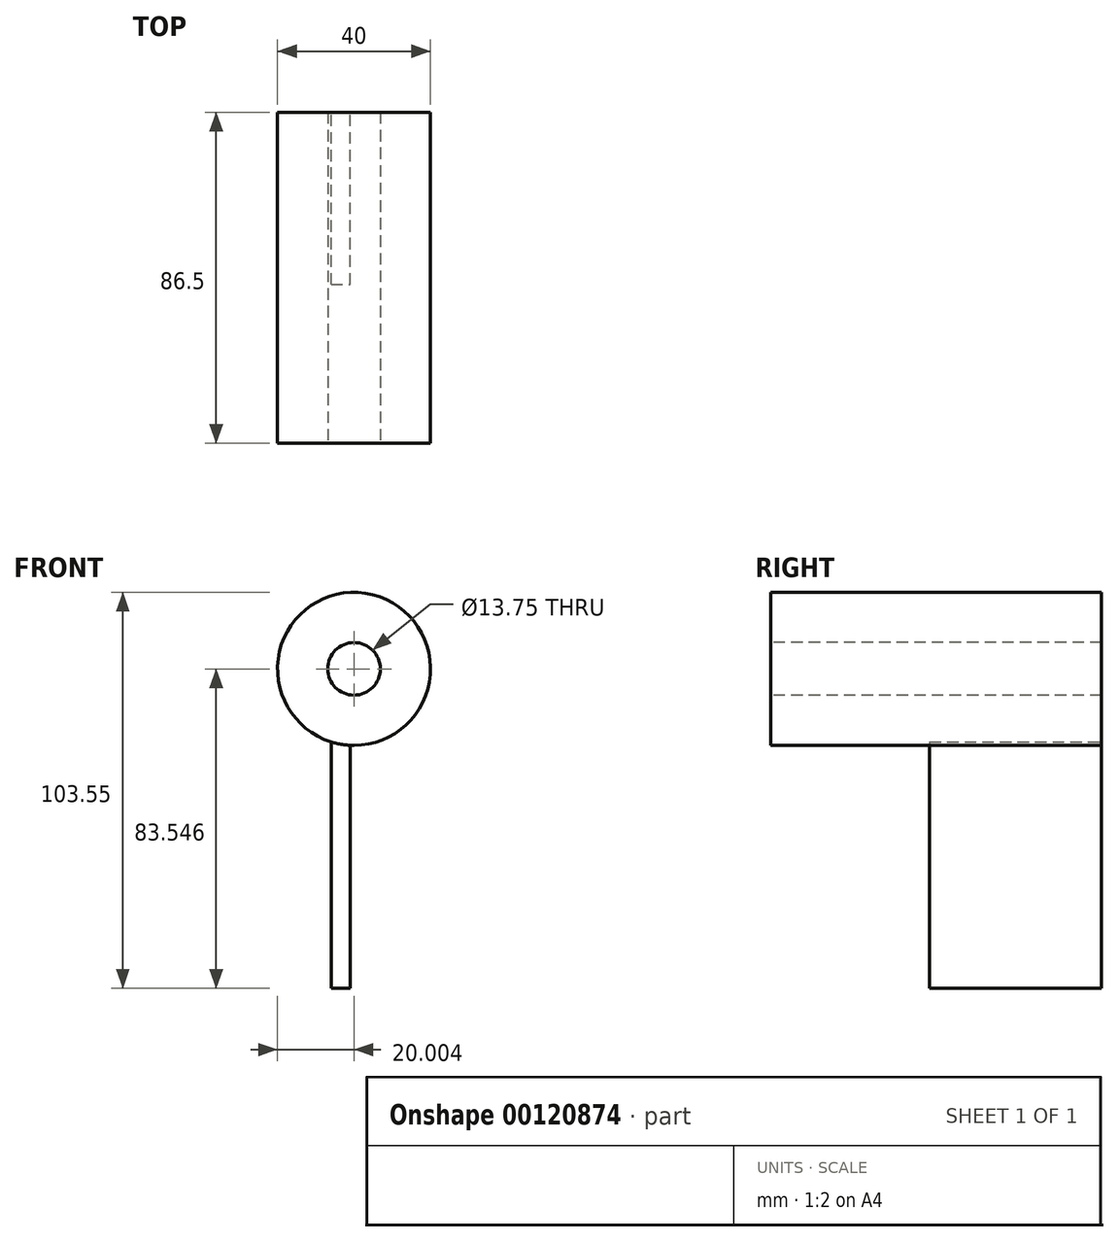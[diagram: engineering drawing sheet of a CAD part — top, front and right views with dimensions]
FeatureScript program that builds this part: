
annotation { "Feature Type Name" : "Feature", "Feature Type Description" : "" }
export const myFeature = defineFeature(function(context is Context, id is Id, definition is map)
    precondition{}
    {
        {
            var Q0;
            Q0=qCreatedBy(makeId("Front.planeOp"),FACE);
            var sketch = newSketch(context, id + "F0", { "sketchPlane" : qUnion([Q0])});
            skCircle(sketch, "E0", {"center": v(-25.19, 35.43) * mm, "radius": 20 * mm});
            skLineSegment(sketch, "E1", {"start": v(-31.14, 16.33) * mm, "end": v(-31.14, -48.12) * mm});
            skLineSegment(sketch, "E2", {"start": v(-31.14, -48.12) * mm, "end": v(-26.14, -48.12) * mm});
            skLineSegment(sketch, "E3", {"start": v(-26.14, -48.12) * mm, "end": v(-26.14, 15.45) * mm});
            skSolve(sketch);
        }
        {
            var Q0;
            {var subQ0=sQuery(id+"F0.wireOp",EDGE,"E0");var subQ1=makeQuery(id+"F0.imprint","INTERSECT",VERTEX,{"derivedFrom":[subQ0,sQuery(id+"F0.wireOp",EDGE,"E1")]});Q0=makeQuery(id+"F0.imprint","IMPRINT",FACE,{"disambiguationData":[TD([[makeQuery(id+"F0.imprint","IMPRINT",EDGE,{"disambiguationData":[TD([[subQ1,-1.0]])],"derivedFrom":subQ0}),1.0]])]});}
            extrude(context, id + "F1", {"entities" : qUnion([Q0]), "depth" : 86.5 * mm});
        }
        {
            var Q0;
            {var subQ0=sQuery(id+"F0.wireOp",EDGE,"E1");Q0=makeQuery(id+"F0.imprint","IMPRINT",FACE,{"disambiguationData":[TD([[makeQuery(id+"F0.imprint","IMPRINT",EDGE,{"derivedFrom":subQ0}),1.0]])]});}
            extrude(context, id + "F2", {"entities" : qUnion([Q0]), "operationType" : NewBodyOperationType.ADD, "depth" : 45 * mm});
        }
        {
            var Q0;
            Q0=makeQuery(id+"F1.opExtrude","CAP_FACE",FACE,{"disambiguationData":[OSD([sQuery(id+"F0.wireOp",EDGE,"E0")])],"isStart":false});
            var sketch = newSketch(context, id + "F3", { "sketchPlane" : qUnion([Q0])});
            skCircle(sketch, "E4", {"center": v(-25.19, 35.43) * mm, "radius": 6.87 * mm});
            skSolve(sketch);
        }
        {
            var Q0;
            Q0=makeQuery(id+"F3.imprint","IMPRINT",FACE,{"disambiguationData":[TD([[makeQuery(id+"F3.imprint","IMPRINT",EDGE,{"derivedFrom":sQuery(id+"F3.wireOp",EDGE,"E4")}),1.0]])]});
            extrude(context, id + "F4", {"entities" : qUnion([Q0]), "operationType" : NewBodyOperationType.REMOVE, "oppositeDirection" : true, "depth" : 100 * mm});
        }
    });
